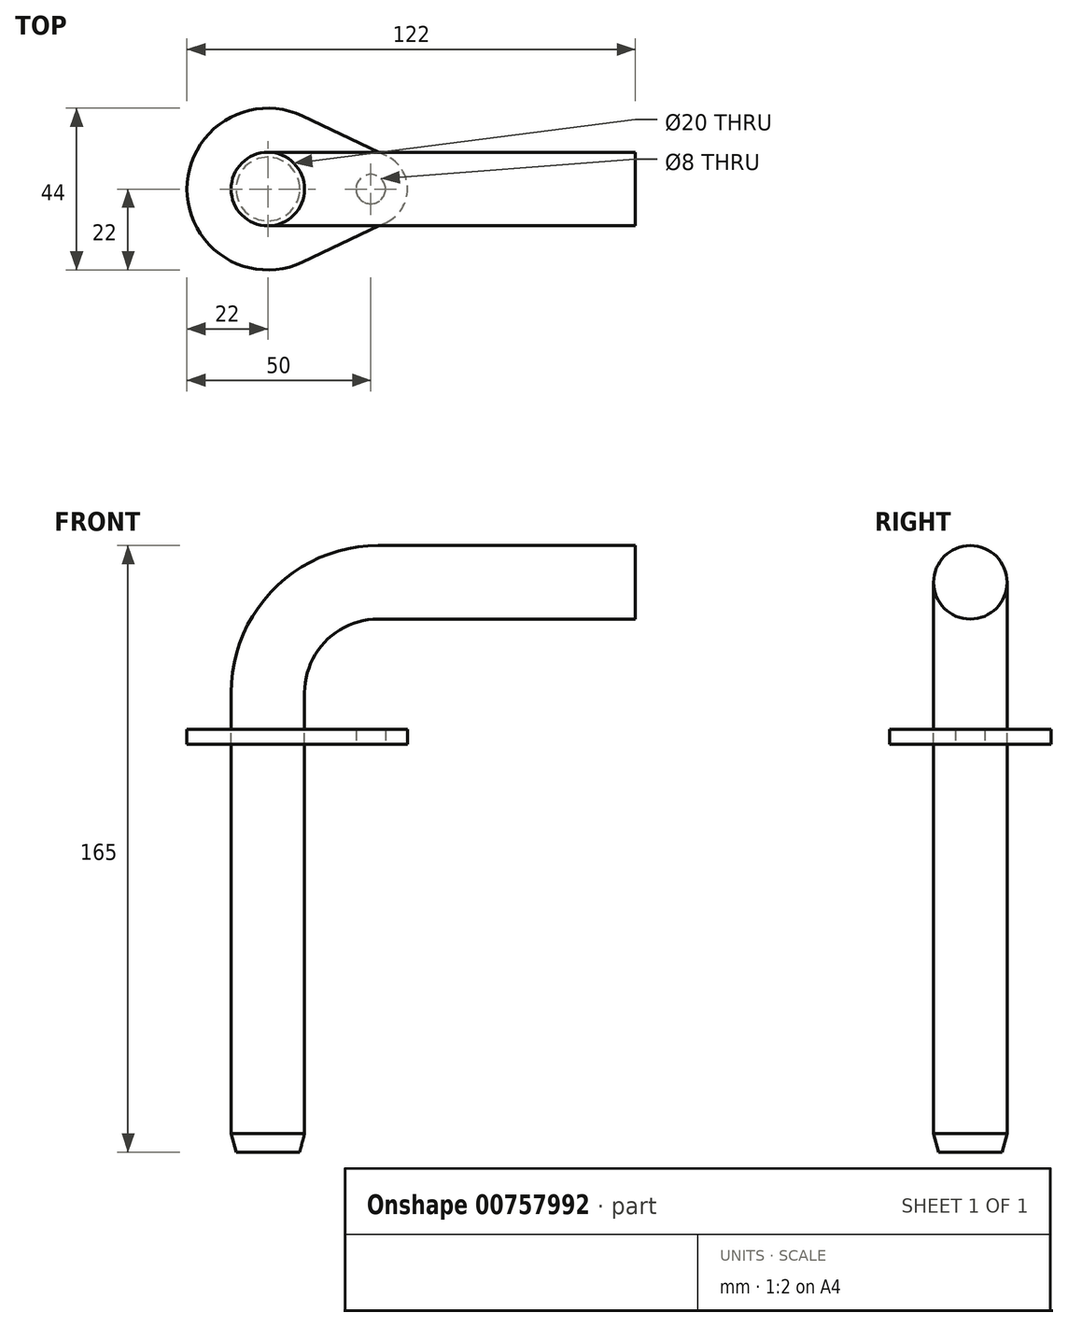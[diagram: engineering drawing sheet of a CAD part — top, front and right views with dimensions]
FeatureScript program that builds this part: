
annotation { "Feature Type Name" : "Feature", "Feature Type Description" : "" }
export const myFeature = defineFeature(function(context is Context, id is Id, definition is map)
    precondition{}
    {
        {
            var Q0;
            Q0=qCreatedBy(makeId("Front.planeOp"),FACE);
            var sketch = newSketch(context, id + "F0", { "sketchPlane" : qUnion([Q0])});
            skLineSegment(sketch, "E0", {"start": v(0, 0) * mm, "end": v(0, 125) * mm});
            skLineSegment(sketch, "E1", {"start": v(30, 155) * mm, "end": v(100, 155) * mm});
            skPoint(sketch, "E2.visualSharp", {"position": v(0, 155) * mm});
            skArc(sketch, "E2.filletArc", {"start": v(30, 155) * mm, "mid": v(8.79, 146.21) * mm, "end": v(0, 125) * mm});
            skSolve(sketch);
        }
        {
            var Q0;
            Q0=qCreatedBy(makeId("Top.planeOp"),FACE);
            var sketch = newSketch(context, id + "F1", { "sketchPlane" : qUnion([Q0])});
            skCircle(sketch, "E3", {"center": v(0, 0) * mm, "radius": 10 * mm});
            skSolve(sketch);
        }
        {
            var Q0;
            Q0=makeQuery(id+"F1.imprint","IMPRINT",FACE,{"disambiguationData":[TD([[makeQuery(id+"F1.imprint","IMPRINT",EDGE,{"derivedFrom":sQuery(id+"F1.wireOp",EDGE,"E3")}),1.0]])]});
            var Q1;
            Q1=sQuery(id+"F0.wireOp",EDGE,"E0");
            var Q2;
            Q2=sQuery(id+"F0.wireOp",EDGE,"E2.filletArc");
            var Q3;
            Q3=sQuery(id+"F0.wireOp",EDGE,"E1");
            sweep(context, id + "F2", {"profiles" : qUnion([Q0]), "path" : qUnion([Q1, Q2, Q3])});
        }
        {
            var Q0;
            Q0=makeQuery(id+"F2.opSweep","CAP_EDGE",EDGE,{"disambiguationData":[OSD([sQuery(id+"F0.wireOp",VERTEX,"E0.start"),sQuery(id+"F1.wireOp",EDGE,"E3")])],"isStart":true});
            chamfer(context, id + "F3", {"entities" : qUnion([Q0]), "chamferType" : ChamferType.OFFSET_ANGLE, "width" : 5 * mm, "oppositeDirection" : false, "angle" : 15 * degree, "tangentPropagation" : true});
        }
        {
            var Q0;
            Q0=qCreatedBy(makeId("Top.planeOp"),FACE);
            cPlane(context, id + "F4", {"entities" : qUnion([Q0]), "cplaneType" : CPlaneType.OFFSET, "offset" : (165 - 54) * mm, "width" : 150 * mm, "height" : 150 * mm});
        }
        {
            var Q0;
            Q0=qCreatedBy(id+"F4.planeOp",FACE);
            var sketch = newSketch(context, id + "F5", { "sketchPlane" : qUnion([Q0])});
            skArc(sketch, "E4", {"start": v(9.43, 19.88) * mm, "mid": v(-22, 0) * mm, "end": v(9.43, -19.88) * mm});
            skArc(sketch, "E5", {"start": v(32.29, -9.04) * mm, "mid": v(38, 0) * mm, "end": v(32.29, 9.04) * mm});
            skLineSegment(sketch, "E6", {"start": v(9.43, 19.88) * mm, "end": v(32.29, 9.04) * mm});
            skLineSegment(sketch, "E7", {"start": v(9.43, -19.88) * mm, "end": v(32.29, -9.04) * mm});
            skCircle(sketch, "E8", {"center": v(0, 0) * mm, "radius": 10 * mm});
            skSolve(sketch);
        }
        {
            var Q0;
            Q0=makeQuery(id+"F5.imprint","IMPRINT",FACE,{"disambiguationData":[TD([[makeQuery(id+"F5.imprint","IMPRINT",EDGE,{"derivedFrom":sQuery(id+"F5.wireOp",EDGE,"E4")}),1.0]])]});
            extrude(context, id + "F6", {"entities" : qUnion([Q0]), "depth" : 4 * mm, "offsetDistance" : 25 * mm});
        }
        {
            var Q0;
            Q0=sQuery(id+"F5.wireOp",VERTEX,"E5.center");
            var Q1;
            Q1=makeQuery(id+"F6.opExtrude","SWEPT_BODY",BODY,{"disambiguationData":[OSD([sQuery(id+"F5.wireOp",EDGE,"E4"),sQuery(id+"F5.wireOp",EDGE,"E5"),sQuery(id+"F5.wireOp",EDGE,"E6"),sQuery(id+"F5.wireOp",EDGE,"E7"),sQuery(id+"F5.wireOp",EDGE,"E8")])]});
            hole(context, id + "F7", {"style" : HoleStyle.SIMPLE, "endStyle" : HoleEndStyle.THROUGH, "oppositeDirection" : true, "holeDiameter" : 8 * mm, "majorDiameter" : 5 * mm, "isTappedThrough" : true, "tappedDepth" : 20 * mm, "tapClearance" : 4, "locations" : qUnion([Q0]), "scope" : qUnion([Q1])});
        }
    });
